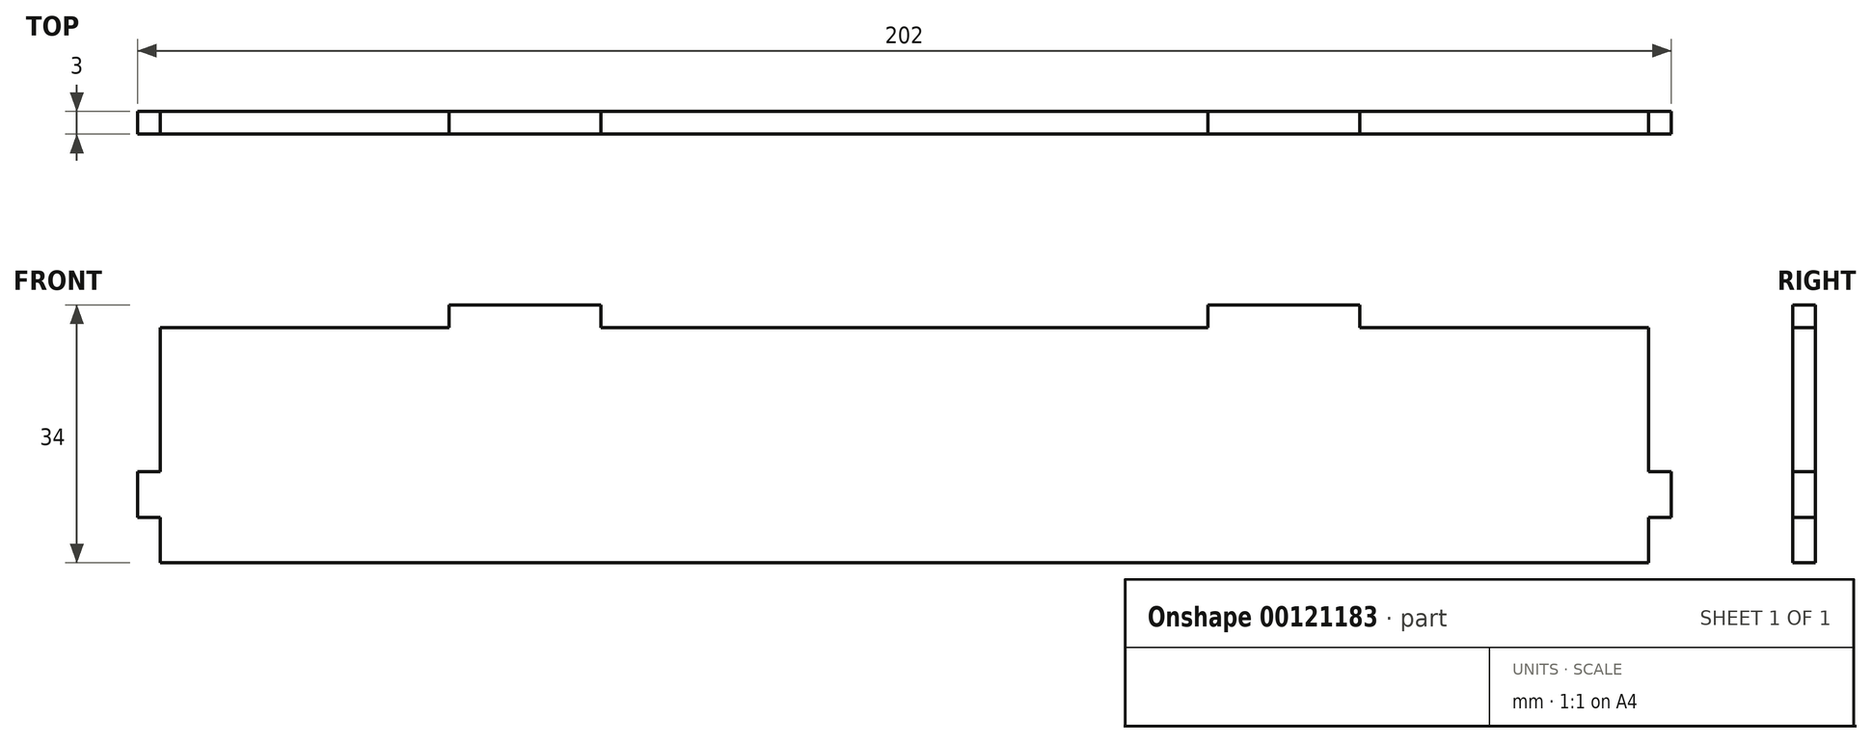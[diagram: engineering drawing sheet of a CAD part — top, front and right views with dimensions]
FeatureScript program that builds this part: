
annotation { "Feature Type Name" : "Feature", "Feature Type Description" : "" }
export const myFeature = defineFeature(function(context is Context, id is Id, definition is map)
    precondition{}
    {
        {
            var Q0;
            Q0=qCreatedBy(makeId("Front.planeOp"),FACE);
            var sketch = newSketch(context, id + "F0", { "sketchPlane" : qUnion([Q0])});
            skLineSegment(sketch, "E0.bottom", {"start": v(-98, 15.5) * mm, "end": v(-60, 15.5) * mm});
            skLineSegment(sketch, "E0.top", {"start": v(-98, -15.5) * mm, "end": v(98, -15.5) * mm});
            skLineSegment(sketch, "E0.left", {"start": v(-98, 15.5) * mm, "end": v(-98, -3.5) * mm});
            skLineSegment(sketch, "E0.right", {"start": v(98, 15.5) * mm, "end": v(98, -3.5) * mm});
            skPoint(sketch, "E0.middle", {"position": v(0, 0) * mm});
            skPoint(sketch, "E1", {"position": v(0, -15.5) * mm});
            skLineSegment(sketch, "E2", {"start": v(0, -15.5) * mm, "end": v(0, 15.5) * mm, "construction": true});
            skLineSegment(sketch, "E3.bottom", {"start": v(40, 18.5) * mm, "end": v(60, 18.5) * mm});
            skLineSegment(sketch, "E3.left", {"start": v(40, 18.5) * mm, "end": v(40, 15.5) * mm});
            skLineSegment(sketch, "E3.right", {"start": v(60, 18.5) * mm, "end": v(60, 15.5) * mm});
            skLineSegment(sketch, "E4.bottom", {"start": v(-40, 18.5) * mm, "end": v(-60, 18.5) * mm});
            skLineSegment(sketch, "E4.left", {"start": v(-40, 18.5) * mm, "end": v(-40, 15.5) * mm});
            skLineSegment(sketch, "E4.right", {"start": v(-60, 18.5) * mm, "end": v(-60, 15.5) * mm});
            skLineSegment(sketch, "E5.top", {"start": v(101, -9.5) * mm, "end": v(98, -9.5) * mm});
            skLineSegment(sketch, "E5.left", {"start": v(101, -3.5) * mm, "end": v(101, -9.5) * mm});
            skLineSegment(sketch, "E6.bottom", {"start": v(-101, -3.5) * mm, "end": v(-98, -3.5) * mm});
            skLineSegment(sketch, "E6.left", {"start": v(-101, -3.5) * mm, "end": v(-101, -9.5) * mm});
            skLineSegment(sketch, "E7", {"start": v(-40, 15.5) * mm, "end": v(0, 15.5) * mm});
            skLineSegment(sketch, "E8", {"start": v(60, 15.5) * mm, "end": v(98, 15.5) * mm});
            skLineSegment(sketch, "E9", {"start": v(0, 15.5) * mm, "end": v(40, 15.5) * mm});
            skLineSegment(sketch, "E10", {"start": v(-98, -9.5) * mm, "end": v(-98, -15.5) * mm});
            skLineSegment(sketch, "E11", {"start": v(98, -9.5) * mm, "end": v(98, -15.5) * mm});
            skLineSegment(sketch, "E12", {"start": v(-98, -9.5) * mm, "end": v(-101, -9.5) * mm});
            skLineSegment(sketch, "E13", {"start": v(101, -3.5) * mm, "end": v(98, -3.5) * mm});
            skSolve(sketch);
        }
        {
            var Q0;
            Q0 = qSketchRegion(id + "F0", true);
            extrude(context, id + "F1", {"entities" : qUnion([Q0]), "endBound" : BoundingType.SYMMETRIC, "depth" : 3 * mm});
        }
    });
